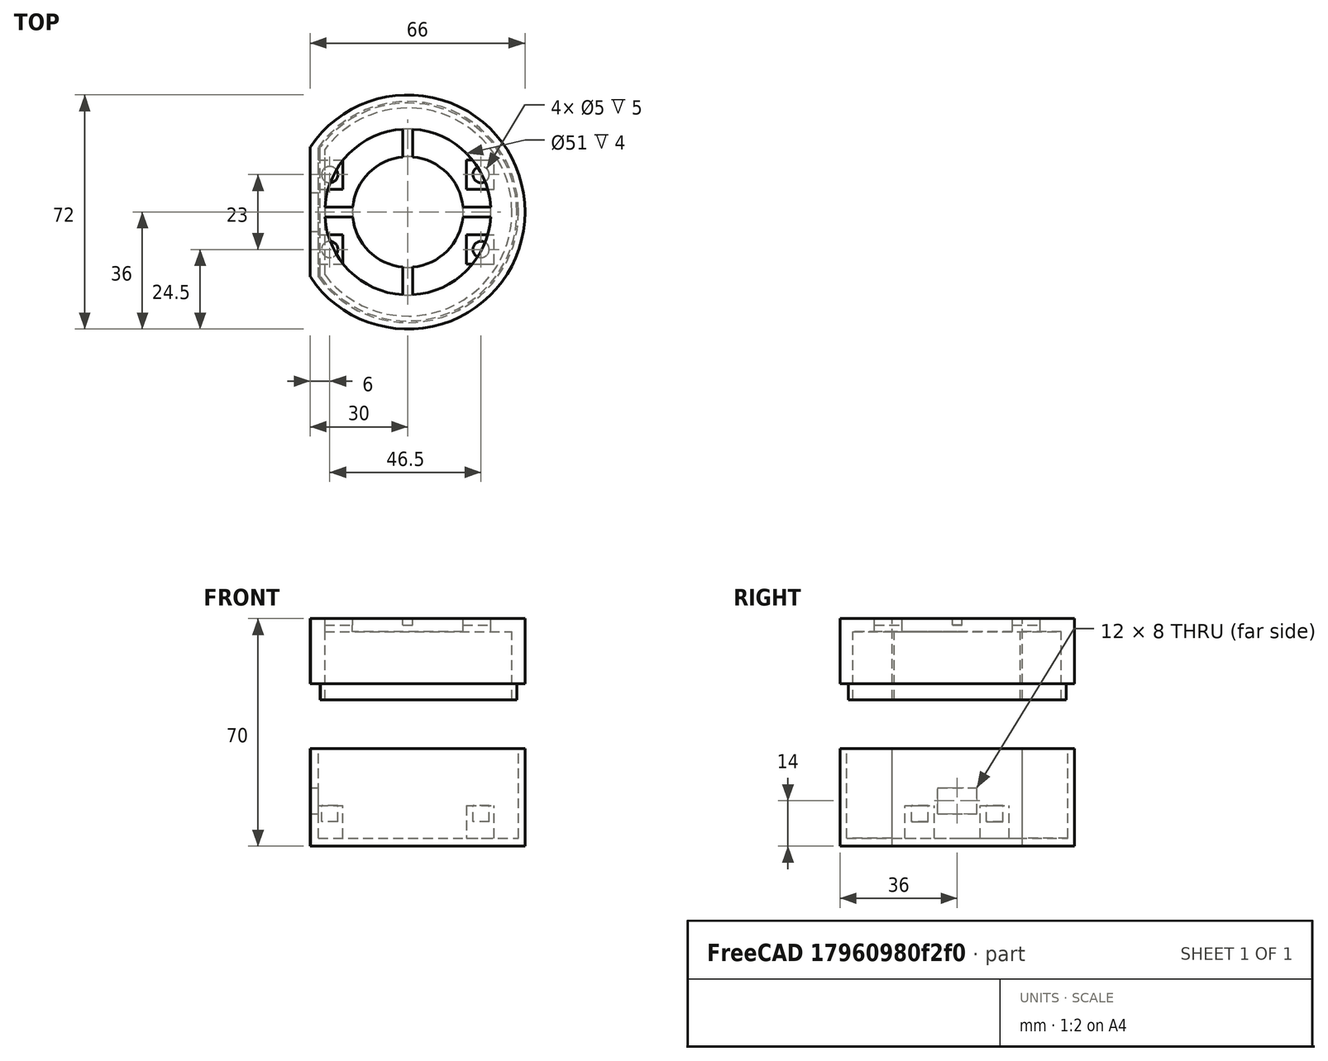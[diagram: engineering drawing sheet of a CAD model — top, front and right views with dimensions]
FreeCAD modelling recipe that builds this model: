
FCSTD DOCUMENT  (FreeCAD 0.16R)
Label: green_tower
License: All rights reserved
LicenseURL: http://en.wikipedia.org/wiki/All_rights_reserved
objects: Part::Cut×14, Part::Cylinder×12, Part::Box×12, Part::MultiFuse×8
note: 46 computed .brp shape members not serialized (recipe doc carries the construction recipe); baked Part::Feature solids carry a one-line shape summary decoded from their .brp

FEATURE [Part::Cylinder] Cylinder  label="Zylinder"
  Angle = 360
  Height = 30
  Radius = 36
FEATURE [Part::Cylinder] Cylinder001  label="Zylinder001"
  Angle = 360
  Height = 30
  Placement = pos=(0,0,2.5) rot=(0,0,1;0rad)
  Radius = 34
FEATURE [Part::Cut] Cut
  Base = -> Cylinder
  Tool = -> Cylinder001
FEATURE [Part::Box] Box  label="Würfel"
  Height = 10
  Length = 54
  Placement = pos=(-27.5,-16,2.5) rot=(0,0,1;0rad)
  Width = 32
FEATURE [Part::Box] Box001  label="Würfel001"
  Height = 50
  Length = 6
  Placement = pos=(-36,-25,0) rot=(0,0,1;0rad)
  Width = 50
FEATURE [Part::Cut] Cut001
  Base = -> Cut
  Tool = -> Box001
FEATURE [Part::Box] Box002  label="Würfel002"
  Height = 30
  Length = 2.5
  Placement = pos=(-30,-20,0) rot=(0,0,1;0rad)
  Width = 40
FEATURE [Part::MultiFuse] Fusion
  Shapes = -> [Cut001,Box002]
FEATURE [Part::Box] Box003  label="Würfel003"
  Height = 8
  Length = 2.5
  Placement = pos=(-30,-6,10) rot=(0,0,1;0rad)
  Width = 12
FEATURE [Part::Cut] Cut002
  Base = -> Fusion
  Tool = -> Box003
FEATURE [Part::Cylinder] Cylinder002  label="Zylinder002"
  Angle = 360
  Height = 5
  Placement = pos=(-24,11.5,7.5) rot=(0,0,1;0rad)
  Radius = 2.5
FEATURE [Part::Cylinder] Cylinder003  label="Zylinder003"
  Angle = 360
  Height = 5
  Placement = pos=(22.5,11.5,7.5) rot=(0,0,1;0rad)
  Radius = 2.5
FEATURE [Part::Cylinder] Cylinder004  label="Zylinder004"
  Angle = 360
  Height = 5
  Placement = pos=(22.5,-11.5,7.5) rot=(0,0,1;0rad)
  Radius = 2.5
FEATURE [Part::Cylinder] Cylinder005  label="Zylinder005"
  Angle = 360
  Height = 5
  Placement = pos=(-24,-11.5,7.5) rot=(0,0,1;0rad)
  Radius = 2.5
FEATURE [Part::Cut] Cut003
  Base = -> Box
  Tool = -> Cylinder002
FEATURE [Part::Cut] Cut004
  Base = -> Cut003
  Tool = -> Cylinder003
FEATURE [Part::Cut] Cut005
  Base = -> Cut004
  Tool = -> Cylinder004
FEATURE [Part::Cut] Cut006
  Base = -> Cut005
  Tool = -> Cylinder005
FEATURE [Part::Box] Box004  label="Würfel004"
  Height = 10
  Length = 54
  Placement = pos=(-27.5,-7,2.5) rot=(0,0,1;0rad)
  Width = 14
FEATURE [Part::Cut] Cut007
  Base = -> Cut006
  Tool = -> Box004
FEATURE [Part::Box] Box005  label="Würfel005"
  Height = 10
  Length = 38
  Placement = pos=(-20,-16,2.5) rot=(0,0,1;0rad)
  Width = 32
FEATURE [Part::Cut] Cut008
  Base = -> Cut007
  Tool = -> Box005
FEATURE [Part::MultiFuse] Fusion001  label="green_tower_bottom"
  Shapes = -> [Cut002,Cut008]
FEATURE [Part::Cylinder] Cylinder006  label="Zylinder006"
  Angle = 360
  Height = 20
  Radius = 36
FEATURE [Part::Cylinder] Cylinder007  label="Zylinder007"
  Angle = 360
  Height = 16
  Radius = 33.5
FEATURE [Part::Cut] Cut009
  Base = -> Cylinder006
  Tool = -> Cylinder007
FEATURE [Part::Cylinder] Cylinder008  label="Zylinder008"
  Angle = 360
  Height = 25
  Placement = pos=(0,0,-5) rot=(0,0,1;0rad)
  Radius = 33.5
FEATURE [Part::Cylinder] Cylinder009  label="Zylinder009"
  Angle = 360
  Height = 25
  Placement = pos=(0,0,-5) rot=(0,0,1;0rad)
  Radius = 32
FEATURE [Part::Cut] Cut010
  Base = -> Cylinder008
  Tool = -> Cylinder009
FEATURE [Part::MultiFuse] Fusion002
  Shapes = -> [Cut009,Cut010]
FEATURE [Part::Box] Box006  label="Würfel006"
  Height = 50
  Length = 10
  Placement = pos=(-40,-25,-20) rot=(0,0,1;0rad)
  Width = 50
FEATURE [Part::Cut] Cut011
  Base = -> Fusion002
  Tool = -> Box006
FEATURE [Part::Box] Box007  label="Würfel007"
  Height = 20
  Length = 3
  Placement = pos=(-30,-20,0) rot=(0,0,1;0rad)
  Width = 40
FEATURE [Part::Box] Box008  label="Würfel008"
  Height = 25
  Length = 1.5
  Placement = pos=(-27,-20,-5) rot=(0,0,1;0rad)
  Width = 40
FEATURE [Part::MultiFuse] Fusion003
  Shapes = -> [Box007,Box008]
FEATURE [Part::MultiFuse] Fusion004
  Shapes = -> [Cut011,Fusion003]
FEATURE [Part::Box] Box009  label="Würfel009"
  Height = 5
  Length = 4
  Placement = pos=(-31,-20,-5) rot=(0,0,1;0rad)
  Width = 40
FEATURE [Part::Cylinder] Cylinder010  label="Zylinder010"
  Angle = 360
  Height = 4
  Placement = pos=(0,0,16) rot=(0,0,1;0rad)
  Radius = 17
FEATURE [Part::Cylinder] Cylinder011  label="Zylinder011"
  Angle = 360
  Height = 4
  Placement = pos=(0,0,16) rot=(0,0,1;0rad)
  Radius = 25.5
FEATURE [Part::Cut] Cut012
  Base = -> Fusion004
  Tool = -> Box009
FEATURE [Part::Cut] Cut013
  Base = -> Cut012
  Tool = -> Cylinder011
FEATURE [Part::Box] Box010  label="Würfel010"
  Height = 2
  Length = 54
  Placement = pos=(-27,-1.5,18) rot=(0,0,1;0rad)
  Width = 3
FEATURE [Part::Box] Box011  label="Würfel011"
  Height = 2
  Length = 54
  Placement = pos=(1.5,-27,18) rot=(0,0,1;1.5708rad)
  Width = 3
FEATURE [Part::MultiFuse] Fusion005
  Shapes = -> [Box010,Box011]
FEATURE [Part::MultiFuse] Fusion006
  Shapes = -> [Cylinder010,Fusion005]
FEATURE [Part::MultiFuse] Fusion007  label="green_tower_top"
  Placement = pos=(0,0,50) rot=(0,0,1;0rad)
  Shapes = -> [Fusion006,Cut013]
